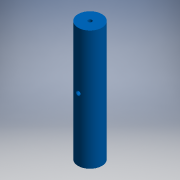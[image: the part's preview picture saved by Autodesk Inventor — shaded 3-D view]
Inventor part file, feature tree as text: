
AUTODESK INVENTOR PART (.ipt)
format: ipt  version: 2016 (Build 200138000, 138)  size: 249,856 bytes
history: native  units: mm (DEFAULTED — no unit token found)
features: extrude x1, sketch x1, other x1
ambient origin geometry x8: Origin, YZ Plane, XZ Plane, XY Plane, X Axis, Y Axis, Z Axis, Center Point
bodies: Solid1 (feature_tree)
feature tree (3):
  extrude  "Extrusion1"  [1 undecoded]
  sketch  "Sketch1"  dims[d0=10.0mm d1=0.0mm]
  other  "0701-001-1-solid1"
note: 1 required parameter value undecoded (feature->parameter linkage not recoverable at this tier; creation-order binding heuristic only, values carry confidence <= 0.55)
